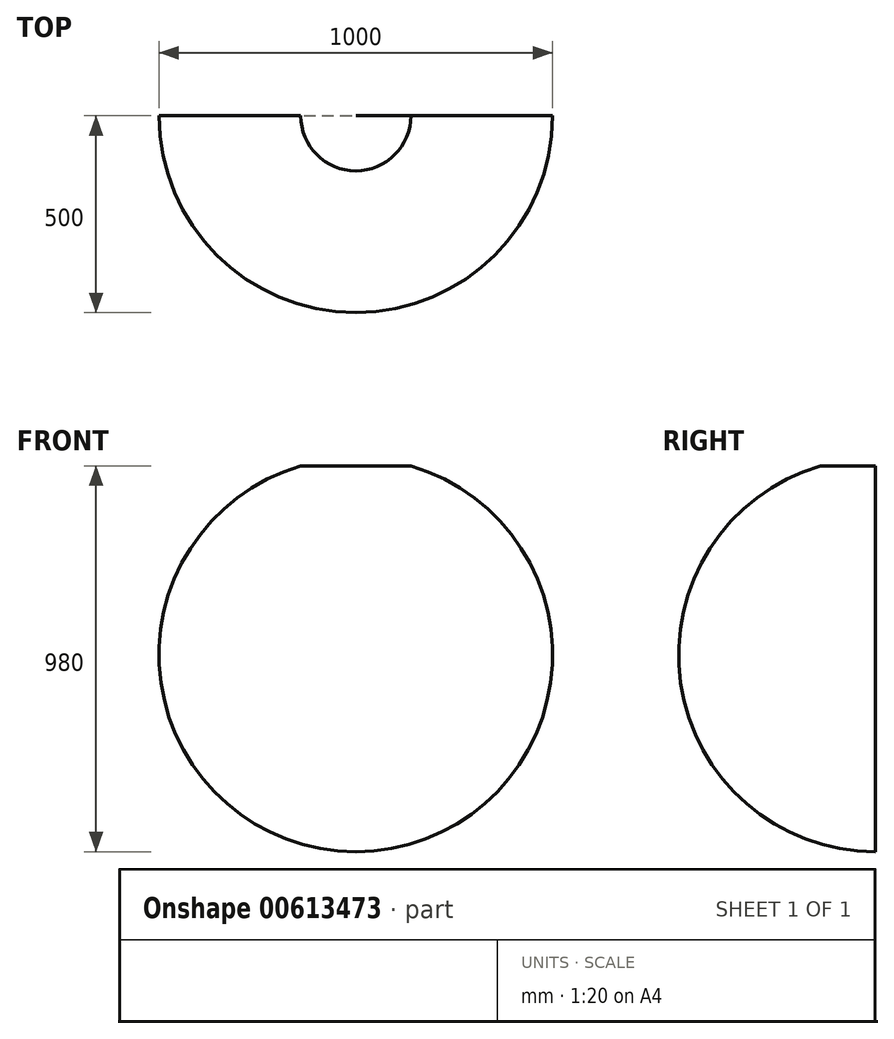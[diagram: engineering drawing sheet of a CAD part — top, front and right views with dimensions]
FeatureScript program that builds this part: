
annotation { "Feature Type Name" : "Feature", "Feature Type Description" : "" }
export const myFeature = defineFeature(function(context is Context, id is Id, definition is map)
    precondition{}
    {
        {
            var Q0;
            Q0=qCreatedBy(makeId("Front.planeOp"),FACE);
            var sketch = newSketch(context, id + "F0", { "sketchPlane" : qUnion([Q0])});
            skPoint(sketch, "E0", {"position": v(0, 0) * mm});
            skLineSegment(sketch, "E1", {"start": v(0, 480) * mm, "end": v(0, -500) * mm});
            skLineSegment(sketch, "E2", {"start": v(140, 480) * mm, "end": v(0, 480) * mm});
            skArc(sketch, "E3", {"start": v(140, 480) * mm, "mid": v(494.97, -70.71) * mm, "end": v(0, -500) * mm});
            skSolve(sketch);
        }
        {
            var Q0;
            Q0=makeQuery(id+"F0.imprint","IMPRINT",FACE,{"disambiguationData":[TD([[makeQuery(id+"F0.imprint","IMPRINT",EDGE,{"derivedFrom":sQuery(id+"F0.wireOp",EDGE,"E1")}),1.0]])]});
            var Q1;
            Q1=sQuery(id+"F0.wireOp",EDGE,"E3");
            var Q2;
            Q2=sQuery(id+"F0.wireOp",EDGE,"E1");
            revolve(context, id + "F1", {"bodyType" : ToolBodyType.SURFACE, "entities" : qUnion([Q0]), "surfaceEntities" : qUnion([Q1]), "axis" : qUnion([Q2]), "revolveType" : RevolveType.ONE_DIRECTION, "angle" : 180 * degree});
        }
    });
